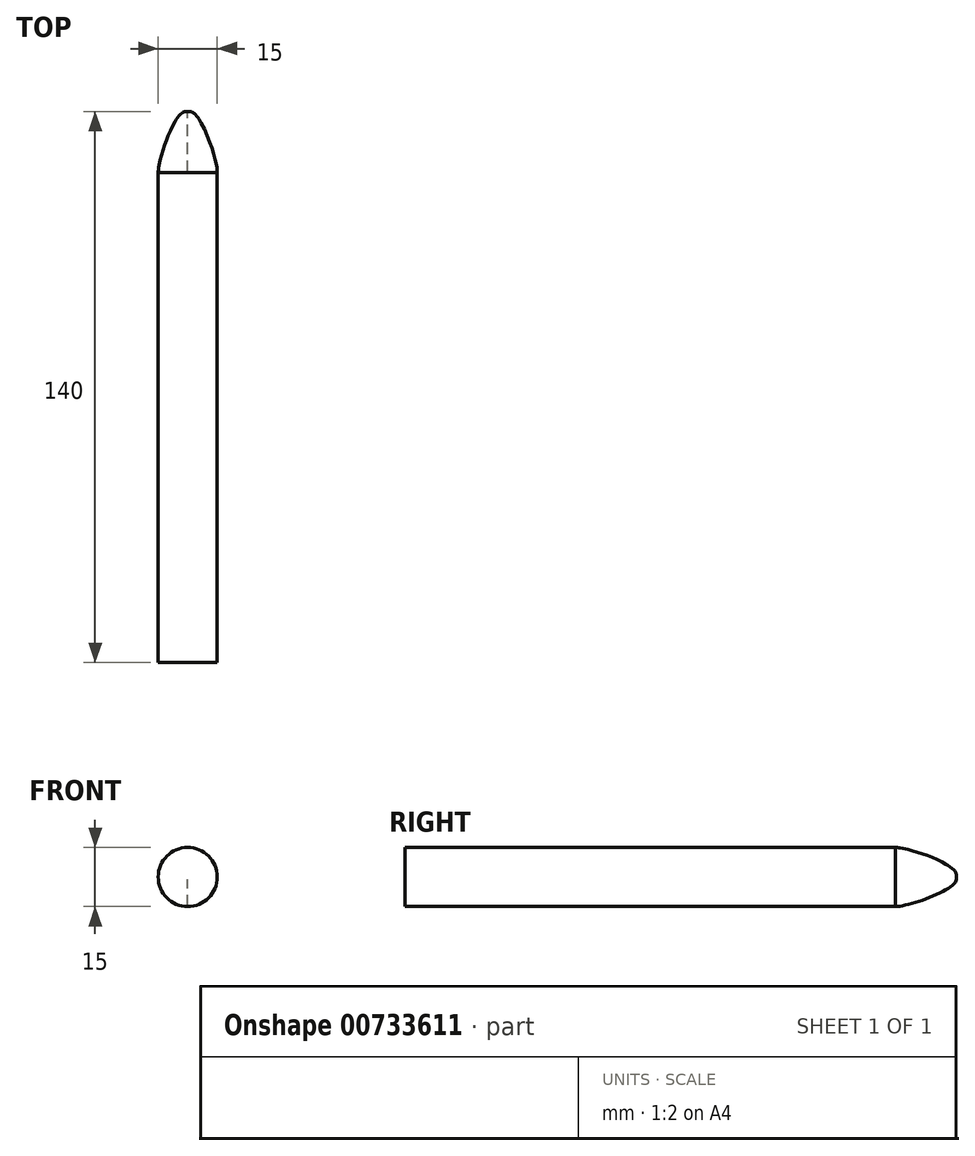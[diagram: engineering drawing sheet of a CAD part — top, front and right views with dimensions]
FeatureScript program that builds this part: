
annotation { "Feature Type Name" : "Feature", "Feature Type Description" : "" }
export const myFeature = defineFeature(function(context is Context, id is Id, definition is map)
    precondition{}
    {
        {
            var Q0;
            Q0=qCreatedBy(makeId("Front.planeOp"),FACE);
            var sketch = newSketch(context, id + "F0", { "sketchPlane" : qUnion([Q0])});
            skCircle(sketch, "E0", {"center": v(0, 0) * mm, "radius": 7.5 * mm});
            skSolve(sketch);
        }
        {
            var Q0;
            Q0 = qSketchRegion(id + "F0", true);
            extrude(context, id + "F1", {"entities" : qUnion([Q0]), "endBound" : BoundingType.SYMMETRIC, "oppositeDirection" : true, "depth" : 140 * mm, "offsetDistance" : 25 * mm});
        }
        {
            var Q0;
            Q0=qCreatedBy(makeId("Right.planeOp"),FACE);
            var sketch = newSketch(context, id + "F2", { "sketchPlane" : qUnion([Q0])});
            skLineSegment(sketch, "E1.0", {"start": v(70, -7.5) * mm, "end": v(70, 7.5) * mm, "construction": true});
            skLineSegment(sketch, "E2", {"start": v(70, 0.63) * mm, "end": v(70, 7.5) * mm});
            skLineSegment(sketch, "E3", {"start": v(70, 7.5) * mm, "end": v(54.5, 7.5) * mm});
            skLineSegment(sketch, "E4", {"start": v(71.22, 0) * mm, "end": v(59.3, 0) * mm, "construction": true});
            skFitSpline(sketch, "E5", {"points": [v(54.5, 7.5) * mm, v(70, 0.63) * mm], "startDerivative": vector(11.57, 0) * mm, "endDerivative": vector(0, -7.74) * mm});
            skSolve(sketch);
        }
        {
            var Q0;
            Q0 = qSketchRegion(id + "F2", true);
            var Q1;
            Q1=sQuery(id+"F2.wireOp",EDGE,"E4");
            revolve(context, id + "F3", {"operationType" : NewBodyOperationType.REMOVE, "surfaceOperationType" : NewSurfaceOperationType.NEW, "entities" : qUnion([Q0]), "axis" : qUnion([Q1]), "revolveType" : RevolveType.FULL, "oppositeDirection" : true});
        }
    });
